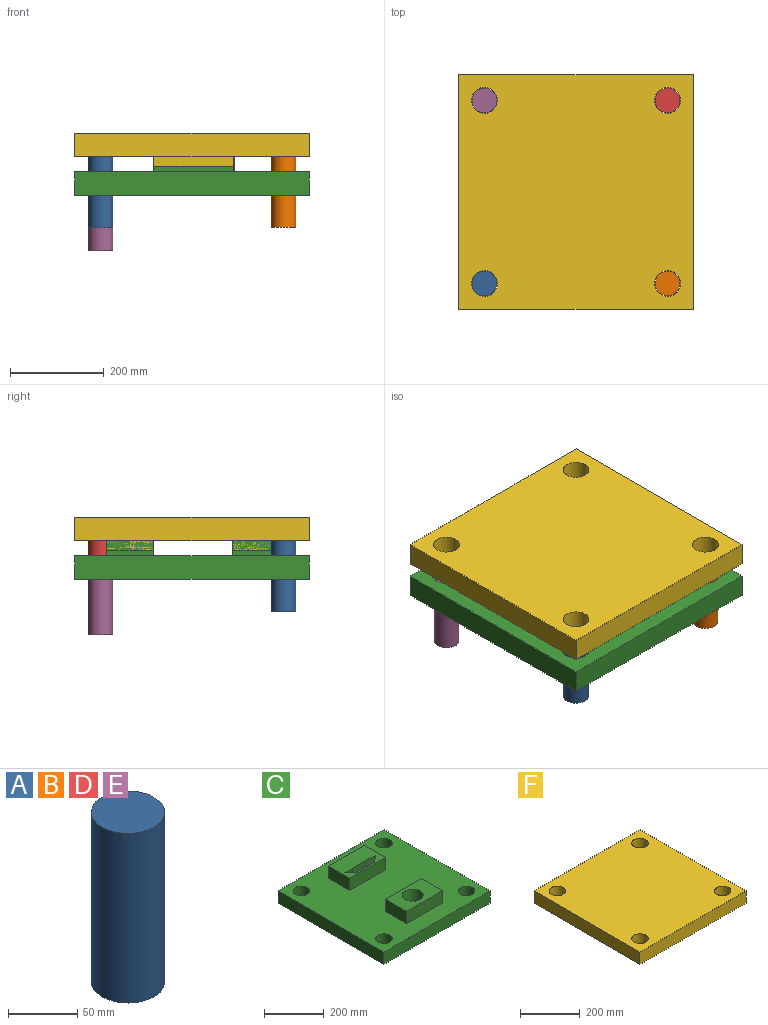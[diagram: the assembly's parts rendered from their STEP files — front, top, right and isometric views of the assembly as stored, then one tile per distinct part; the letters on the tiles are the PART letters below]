
ASSEMBLY  parts=6 mates=5
PART A: 3 faces, bbox 53x53x150 mm
  f0: plane 53x53mm, normal (0,0,1), area 2206.2mm2, adj f2
  f1: plane 53x53mm, normal (0,0,-1), area 2206.2mm2, adj f2
  f2: cylinder r=26.5mm len=150mm, axis (0,0,1), area 24975.7mm2, adj f0,f1
PART B: same geometry as A
PART C: 27 faces, bbox 500x500x100 mm
  f0: plane 500x50mm, normal (0,1,0), area 25000mm2, adj f1,f7,f8,f9
  f1: plane 500x50mm, normal (-1,0,0), area 25000mm2, adj f0,f2,f8,f9
  f2: plane 500x50mm, normal (0,-1,0), area 25000mm2, adj f1,f7,f8,f9
  f3: cylinder r=27.5mm len=55mm, axis (0,0,-1), area 8639.4mm2, adj f8,f9
  f4: cylinder r=27.5mm len=55mm, axis (0,0,-1), area 8639.4mm2, adj f8,f9
  f5: cylinder r=27.5mm len=55mm, axis (0,0,-1), area 8639.4mm2, adj f8,f9
  f6: cylinder r=27.5mm len=55mm, axis (0,0,-1), area 8639.4mm2, adj f8,f9
  f7: plane 500x50mm, normal (1,0,0), area 25000mm2, adj f0,f2,f8,f9
  f8: plane 500x500mm, normal (0,0,1), area 206496.7mm2, adj f0,f1,f2,f3,f4,f5,f6,f7
  f9: plane 500x500mm, normal (0,0,-1), area 235352.1mm2, adj f0,f1,f2,f3,f4,f5,f6,f7
  f10: plane 170x50mm, normal (0,1,0), area 8500mm2, adj f8,f11,f19,f20
  f11: plane 100x50mm, normal (-1,0,0), area 5000mm2, adj f8,f10,f12,f20
  f12: plane 170x50mm, normal (0,-1,0), area 8500mm2, adj f8,f11,f19,f20
  f13: plane 100x64.51mm, normal (0.01,-1,0), area 6452mm2, adj f9,f14,f18,f20
  f14: plane 100x43.64mm, normal (-0.09,-1,0), area 4380.6mm2, adj f9,f13,f15,f20
  f15: plane 100x31.31mm, normal (-0.59,0.81,0), area 3871.2mm2, adj f9,f14,f16,f20
  f16: plane 100x85.38mm, normal (0,1,0), area 8538.5mm2, adj f9,f15,f17,f20
  f17: plane 100x27.51mm, normal (0.68,0.73,0), area 3759.1mm2, adj f9,f16,f18,f20
  f18: plane 100x36.05mm, normal (0,-1,0), area 3605.1mm2, adj f9,f13,f17,f20
  f19: plane 100x50mm, normal (1,0,0), area 5000mm2, adj f8,f10,f12,f20
  f20: plane 170x100mm, normal (0,0,1), area 14025.7mm2, adj f10,f11,f12,f13,f14,f15,f16,f17
  f21: plane 170x50mm, normal (0,1,0), area 8500mm2, adj f8,f22,f25,f26
  f22: plane 100x50mm, normal (-1,0,0), area 5000mm2, adj f8,f21,f23,f26
  f23: plane 170x50mm, normal (0,-1,0), area 8500mm2, adj f8,f22,f25,f26
  f24: cone r=35.03mm half-angle=5deg, axis (0,0,1), area 19336.7mm2, adj f9,f26
  f25: plane 100x50mm, normal (1,0,0), area 5000mm2, adj f8,f21,f23,f26
  f26: plane 170x100mm, normal (0,0,1), area 13144.4mm2, adj f21,f22,f23,f24,f25
PART D: same geometry as A
PART E: same geometry as A
PART F: 29 faces, bbox 500x500x121 mm
  f0: plane 500x50mm, normal (0,1,0), area 25000mm2, adj f1,f7,f8,f9
  f1: plane 500x50mm, normal (-1,0,0), area 25000mm2, adj f0,f2,f8,f9
  f2: plane 500x50mm, normal (0,-1,0), area 25000mm2, adj f1,f7,f8,f9
  f3: cylinder r=27.5mm len=55mm, axis (0,0,1), area 8639.4mm2, adj f8,f9
  f4: cylinder r=27.5mm len=55mm, axis (0,0,1), area 8639.4mm2, adj f8,f9
  f5: cylinder r=27.5mm len=55mm, axis (0,0,1), area 8639.4mm2, adj f8,f9
  f6: cylinder r=27.5mm len=55mm, axis (0,0,1), area 8639.4mm2, adj f8,f9
  f7: plane 500x50mm, normal (1,0,0), area 25000mm2, adj f0,f2,f8,f9
  f8: plane 500x500mm, normal (0,0,-1), area 206496.7mm2, adj f0,f1,f2,f3,f4,f5,f6,f7
  f9: plane 500x500mm, normal (0,0,1), area 240496.7mm2, adj f0,f1,f2,f3,f4,f5,f6,f7
  f10: plane 170x100mm, normal (0,0,-1), area 14025.7mm2, adj f11,f12,f13,f14,f20,f21,f22,f23
  f11: plane 100x20mm, normal (1,0,0), area 2000mm2, adj f8,f10,f12,f14
  f12: plane 170x20mm, normal (0,-1,0), area 3400mm2, adj f8,f10,f11,f13
  f13: plane 100x20mm, normal (-1,0,0), area 2000mm2, adj f8,f10,f12,f14
  f14: plane 170x20mm, normal (0,1,0), area 3400mm2, adj f8,f10,f11,f13
  f15: plane 170x100mm, normal (0,0,-1), area 13144.4mm2, adj f16,f17,f18,f19,f27
  f16: plane 100x20mm, normal (1,0,0), area 2000mm2, adj f8,f15,f17,f19
  f17: plane 170x20mm, normal (0,-1,0), area 3400mm2, adj f8,f15,f16,f18
  f18: plane 100x20mm, normal (-1,0,0), area 2000mm2, adj f8,f15,f17,f19
  f19: plane 170x20mm, normal (0,1,0), area 3400mm2, adj f8,f15,f16,f18
  f20: plane 51x43.64mm, normal (-0.09,1,0), area 2234.1mm2, adj f10,f21,f25,f26
  f21: plane 51x31.31mm, normal (-0.59,-0.81,0), area 1974.3mm2, adj f10,f20,f22,f26
  f22: plane 85.38x51mm, normal (0,-1,0), area 4354.6mm2, adj f10,f21,f23,f26
  f23: plane 51x27.51mm, normal (0.68,-0.73,0), area 1917.2mm2, adj f10,f22,f24,f26
  f24: plane 51x36.05mm, normal (0,1,0), area 1838.6mm2, adj f10,f23,f25,f26
  f25: plane 64.51x51mm, normal (0.01,1,0), area 3290.5mm2, adj f10,f20,f24,f26
  f26: plane 144.21x26.56mm, normal (0,0,-1), area 2974.3mm2, adj f20,f21,f22,f23,f24,f25
  f27: cylinder r=35.03mm len=70.07mm, axis (0,0,1), area 11226mm2, adj f15,f28
  f28: plane 70.07x70.07mm, normal (0,0,-1), area 3855.6mm2, adj f27
PLACE A t=(-329,-516.58,155.31)mm
PLACE B t=(61,-516.58,155.31)mm
PLACE C t=(-238.97,-321.58,179.39)mm
PLACE D t=(61,-126.58,155.31)mm
PLACE E t=(-329,-126.58,105.31)mm
PLACE F t=(-238.97,-321.58,311.47)mm
MATE slider B.f2 <-> C.f5  axis (0,0,-1) through (-43.97,-516.58,111.47)mm
MATE slider A.f2 <-> C.f4  axis (0,0,-1) through (-433.97,-516.58,111.47)mm
MATE slider F.f5 <-> B.f2  axis (0,0,1) through (-43.97,-516.58,261.47)mm
MATE slider D.f2 <-> C.f6  axis (0,0,-1) through (-43.97,-126.58,111.47)mm
MATE slider C.f3 <-> E.f2  axis (0,0,-1) through (-433.97,-126.58,179.39)mm
